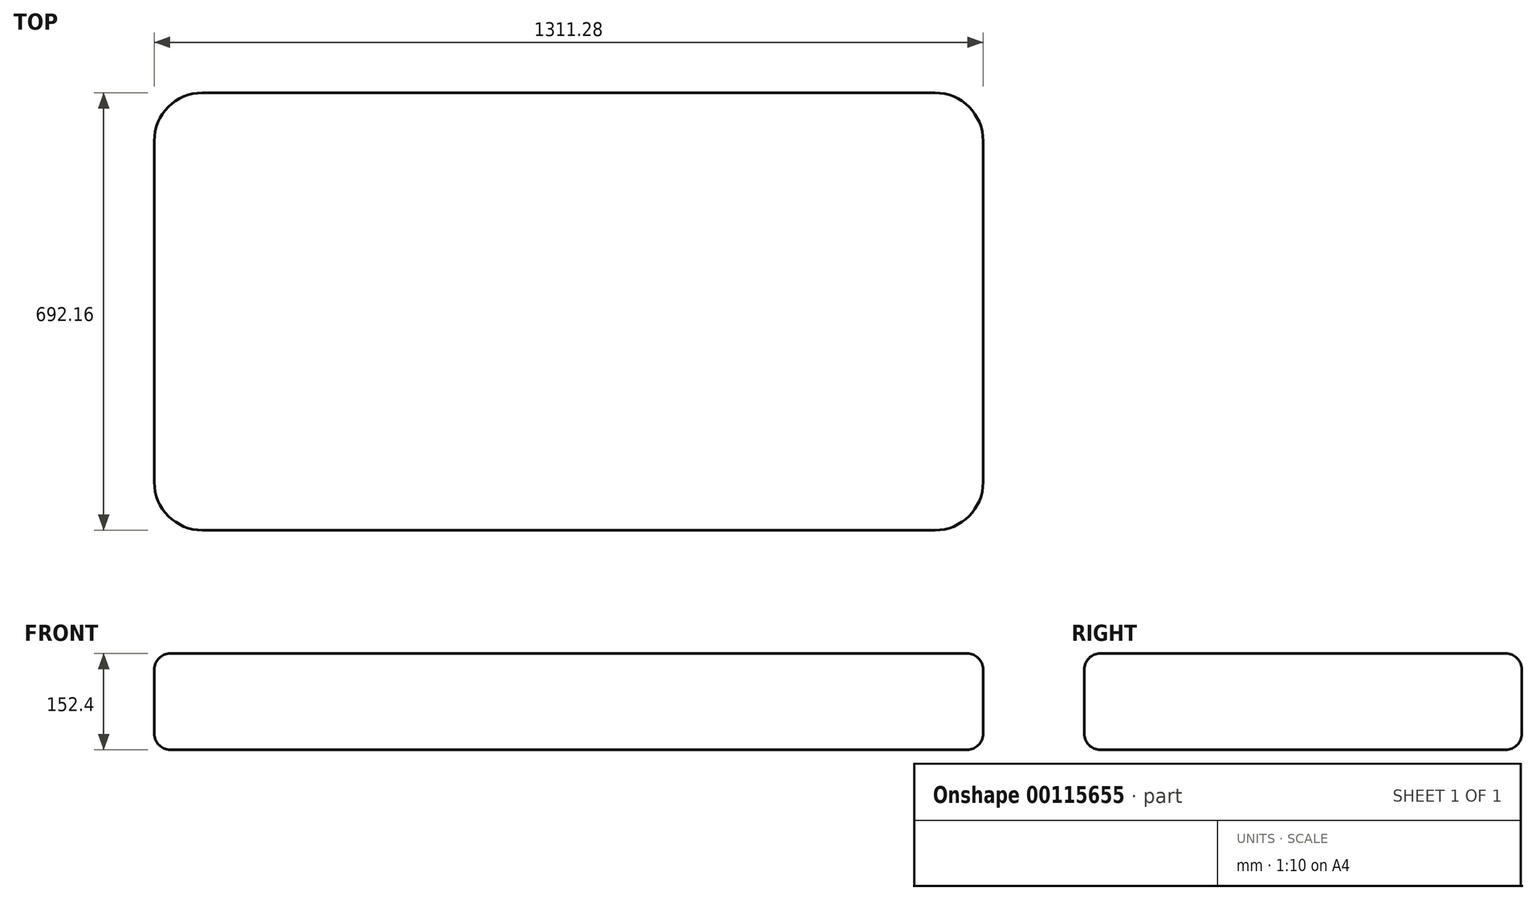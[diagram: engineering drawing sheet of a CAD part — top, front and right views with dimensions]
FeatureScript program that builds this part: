
annotation { "Feature Type Name" : "Feature", "Feature Type Description" : "" }
export const myFeature = defineFeature(function(context is Context, id is Id, definition is map)
    precondition{}
    {
        {
            var Q0;
            Q0=qCreatedBy(makeId("Top.planeOp"),FACE);
            var sketch = newSketch(context, id + "F0", { "sketchPlane" : qUnion([Q0])});
            skLineSegment(sketch, "E0.bottom", {"start": v(579.44, 346.08) * mm, "end": v(-579.44, 346.08) * mm});
            skLineSegment(sketch, "E0.top", {"start": v(579.44, -346.08) * mm, "end": v(-579.44, -346.08) * mm});
            skLineSegment(sketch, "E0.left", {"start": v(655.64, 269.88) * mm, "end": v(655.64, -269.88) * mm});
            skLineSegment(sketch, "E0.right", {"start": v(-655.64, 269.88) * mm, "end": v(-655.64, -269.88) * mm});
            skPoint(sketch, "E0.middle", {"position": v(0, 0) * mm});
            skPoint(sketch, "E1.visualSharp", {"position": v(-655.64, -346.08) * mm});
            skArc(sketch, "E1.filletArc", {"start": v(-655.64, -269.88) * mm, "mid": v(-633.32, -323.76) * mm, "end": v(-579.44, -346.08) * mm});
            skPoint(sketch, "E2.visualSharp", {"position": v(655.64, -346.08) * mm});
            skArc(sketch, "E2.filletArc", {"start": v(579.44, -346.08) * mm, "mid": v(633.32, -323.76) * mm, "end": v(655.64, -269.88) * mm});
            skPoint(sketch, "E3.visualSharp", {"position": v(655.64, 346.08) * mm});
            skArc(sketch, "E3.filletArc", {"start": v(655.64, 269.88) * mm, "mid": v(633.32, 323.76) * mm, "end": v(579.44, 346.08) * mm});
            skPoint(sketch, "E4.visualSharp", {"position": v(-655.64, 346.08) * mm});
            skArc(sketch, "E4.filletArc", {"start": v(-579.44, 346.08) * mm, "mid": v(-633.32, 323.76) * mm, "end": v(-655.64, 269.88) * mm});
            skSolve(sketch);
        }
        {
            var Q0;
            Q0 = qSketchRegion(id + "F0", true);
            extrude(context, id + "F1", {"entities" : qUnion([Q0]), "depth" : 152.4 * mm});
        }
        {
            var Q0;
            Q0=makeQuery(id+"F1.opExtrude","CAP_EDGE",EDGE,{"disambiguationData":[OSD([sQuery(id+"F0.wireOp",EDGE,"E0.top")])],"isStart":false});
            var Q1;
            Q1=makeQuery(id+"F1.opExtrude","CAP_EDGE",EDGE,{"disambiguationData":[OSD([sQuery(id+"F0.wireOp",EDGE,"E0.top")])],"isStart":true});
            fillet(context, id + "F2", {"entities" : qUnion([Q0, Q1]), "radius" : 25.4 * mm, "tangentPropagation" : true, "allowEdgeOverflow" : false});
        }
    });
